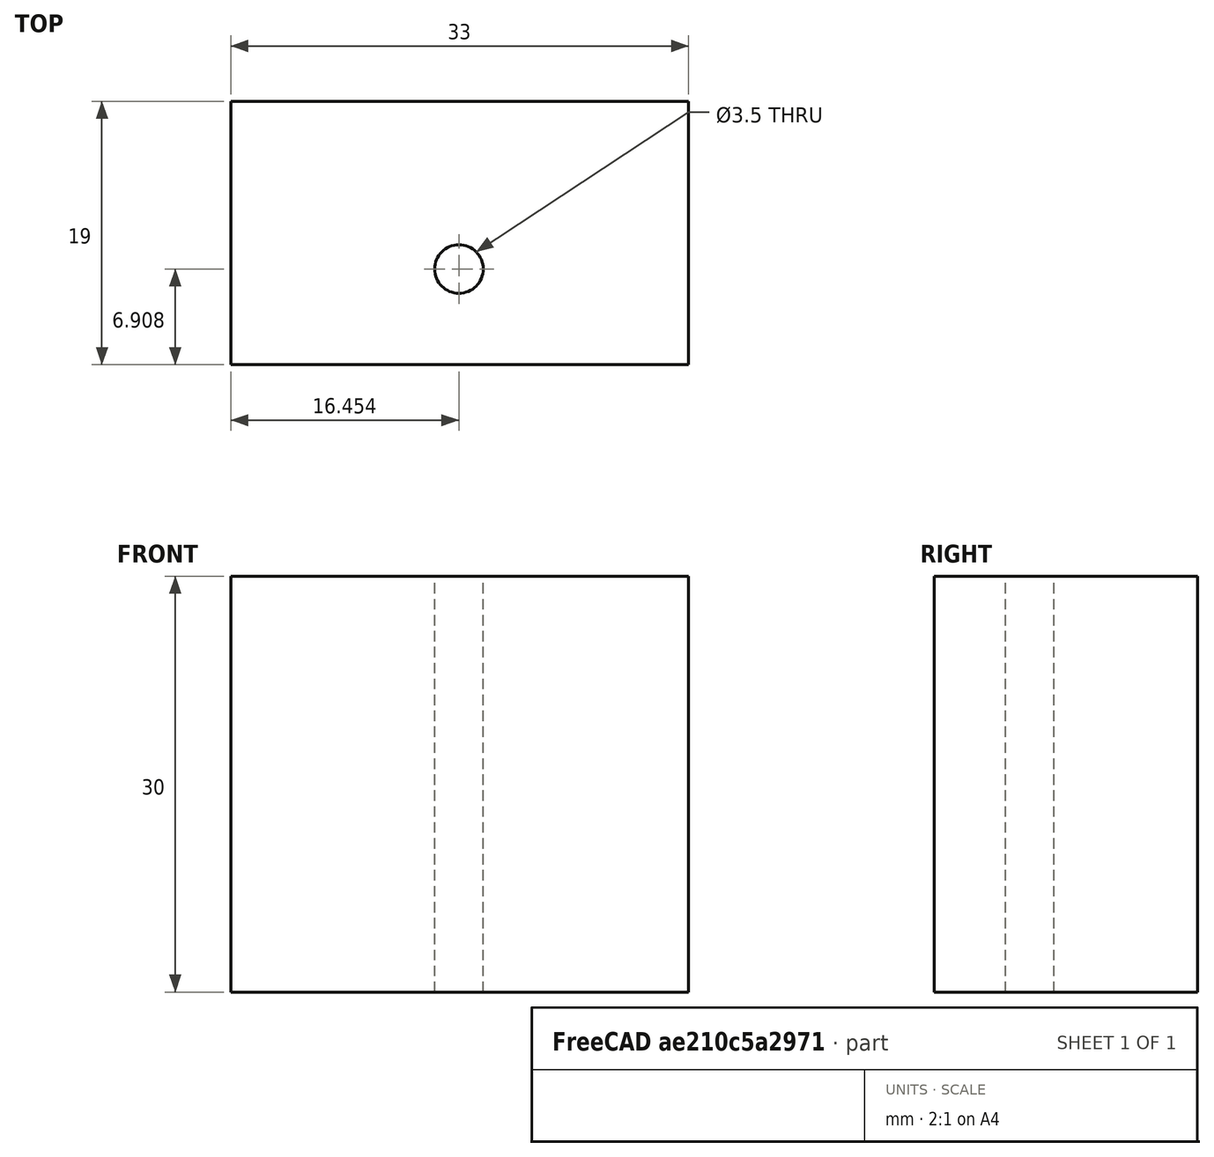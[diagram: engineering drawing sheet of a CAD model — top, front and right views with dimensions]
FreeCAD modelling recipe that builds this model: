
FCSTD DOCUMENT  (FreeCAD 0.19R24267 +148 (Git))
Label: hoppper
License: All rights reserved
LicenseURL: http://en.wikipedia.org/wiki/All_rights_reserved
objects: Sketcher::SketchObject×2, Part::Box×1, PartDesign::FeatureBase×1, PartDesign::Plane×1, PartDesign::Hole×1, PartDesign::Body×1
note: 8 computed .brp shape members not serialized (recipe doc carries the construction recipe); baked Part::Feature solids carry a one-line shape summary decoded from their .brp

FEATURE [Part::Box] Box  label="Cube"
  AttacherType = Attacher::AttachEngine3D
  Height = 30
  Length = 33
  Width = 19
FEATURE [PartDesign::FeatureBase] BaseFeature
  BaseFeature = -> Box
FEATURE [PartDesign::Plane] DatumPlane
  Length = 68.7703
  MapMode = 5
  Placement = pos=(0,0,0) rot=(1,0,0;3.14159rad)
  ResizeMode = 0
  Support = -> [BaseFeature]
  Width = 60.7703
FEATURE [Sketcher::SketchObject] Sketch
  FullyConstrained = false
  MapMode = 5
  Placement = pos=(0,0,0) rot=(1,0,0;3.14159rad)
  Support = -> [DatumPlane]
  sketch-geometry (1):
    g0: Circle CenterX=16.4537 CenterY=-6.90815 CenterZ=0 NormalX=0 NormalY=0 NormalZ=1 AngleXU=0 Radius=2.01803
FEATURE [PartDesign::Hole] Hole
  BaseFeature = -> BaseFeature
  Depth = 25
  DepthType = 1
  Diameter = 3.5
  DrillForDepth = false
  DrillPoint = 1
  DrillPointAngle = 118
  HoleCutCountersinkAngle = 90
  HoleCutCustomValues = false
  HoleCutDepth = 0
  HoleCutDiameter = 6.1
  HoleCutType = 0
  ModelActualThread = false
  Profile = -> Sketch
  Tapered = false
  TaperedAngle = 90
  ThreadAngle = 0
  ThreadClass = 0
  ThreadCutOffInner = 0
  ThreadCutOffOuter = 0
  ThreadDirection = 0
  ThreadFit = 0
  ThreadPitch = 0
  ThreadSize = 0
  ThreadType = 0
  Threaded = false
  expr: Diameter = 3.5
FEATURE [Sketcher::SketchObject] Sketch001
  FullyConstrained = true
  MapMode = 5
  Placement = pos=(0,0,0) rot=(1,0,0;3.14159rad)
  Support = -> [DatumPlane]
FEATURE [PartDesign::Body] Body
  BaseFeature = -> Box
  Group = -> [BaseFeature,DatumPlane,Sketch,Hole,Sketch001]
  Origin = -> Origin
  Tip = -> Hole
